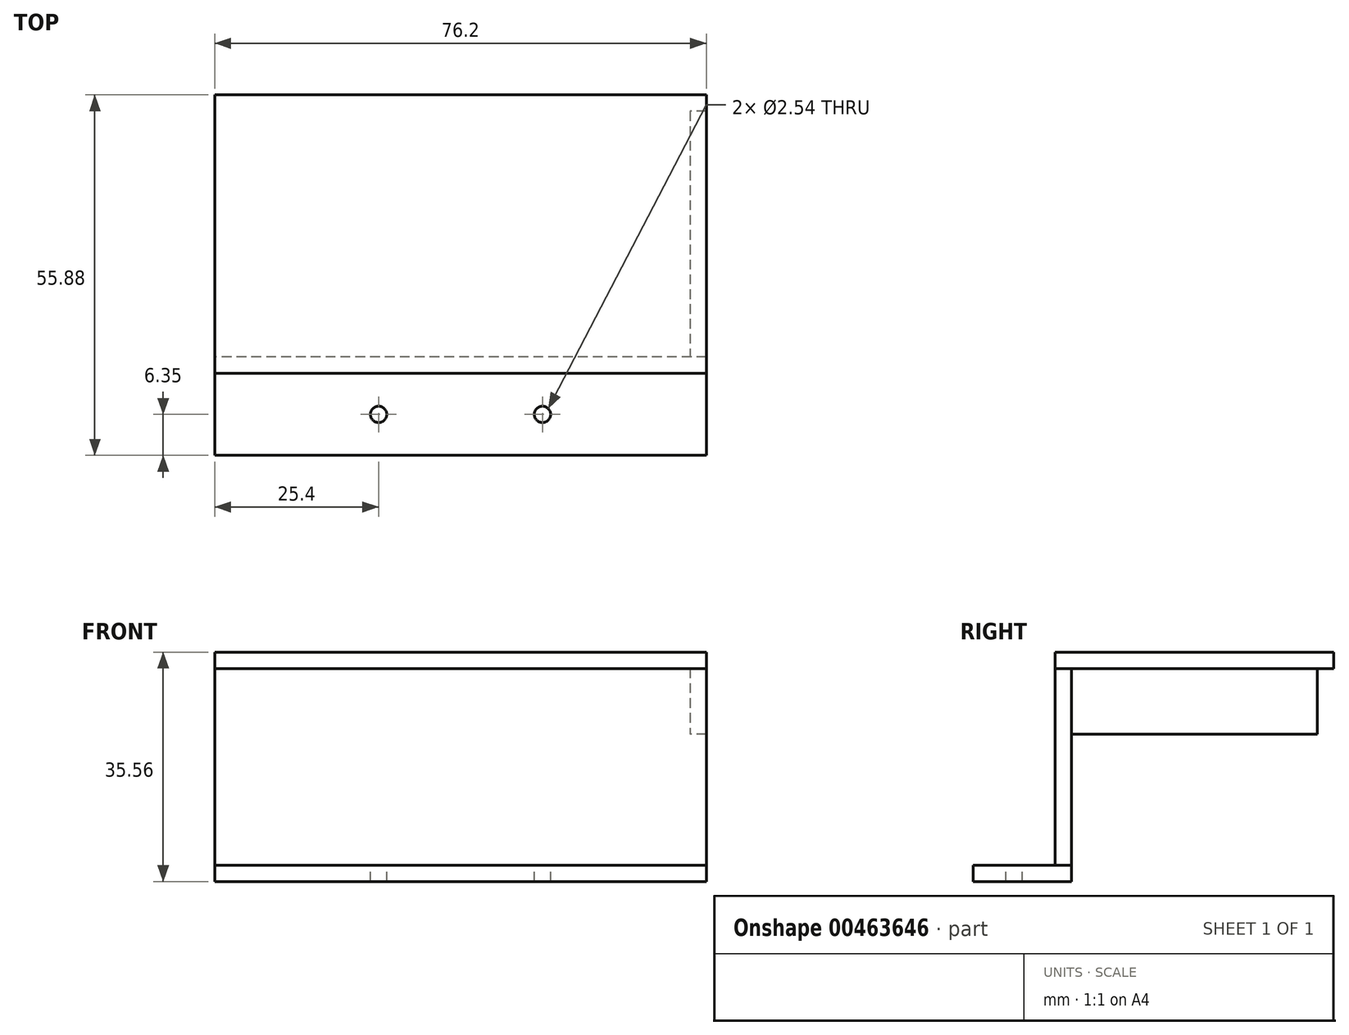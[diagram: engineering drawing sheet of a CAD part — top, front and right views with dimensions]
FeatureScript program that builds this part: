
annotation { "Feature Type Name" : "Feature", "Feature Type Description" : "" }
export const myFeature = defineFeature(function(context is Context, id is Id, definition is map)
    precondition{}
    {
        {
            var Q0;
            Q0=qCreatedBy(makeId("Front.planeOp"),FACE);
            var sketch = newSketch(context, id + "F0", { "sketchPlane" : qUnion([Q0])});
            skLineSegment(sketch, "E0.bottom", {"start": v(38.1, -15.24) * mm, "end": v(-38.1, -15.24) * mm});
            skLineSegment(sketch, "E0.top", {"start": v(38.1, 15.24) * mm, "end": v(-38.1, 15.24) * mm});
            skLineSegment(sketch, "E0.left", {"start": v(38.1, -15.24) * mm, "end": v(38.1, 15.24) * mm});
            skLineSegment(sketch, "E0.right", {"start": v(-38.1, -15.24) * mm, "end": v(-38.1, 15.24) * mm});
            skPoint(sketch, "E0.middle", {"position": v(0, 0) * mm});
            skSolve(sketch);
        }
        {
            var Q0;
            Q0=makeQuery(id+"F0.imprint","IMPRINT",FACE,{"disambiguationData":[TD([[makeQuery(id+"F0.imprint","IMPRINT",EDGE,{"derivedFrom":sQuery(id+"F0.wireOp",EDGE,"E0.bottom")}),-1.0]])]});
            extrude(context, id + "F1", {"entities" : qUnion([Q0]), "depth" : 2.54 * mm});
        }
        {
            var Q0;
            Q0=qCreatedBy(makeId("Right.planeOp"),FACE);
            var sketch = newSketch(context, id + "F2", { "sketchPlane" : qUnion([Q0])});
            skLineSegment(sketch, "E1.bottom", {"start": v(21.59, -5.08) * mm, "end": v(-21.59, -5.08) * mm});
            skLineSegment(sketch, "E1.top", {"start": v(21.59, 5.08) * mm, "end": v(-21.59, 5.08) * mm});
            skLineSegment(sketch, "E1.left", {"start": v(21.59, -5.08) * mm, "end": v(21.59, 5.08) * mm});
            skLineSegment(sketch, "E1.right", {"start": v(-21.59, -5.08) * mm, "end": v(-21.59, 5.08) * mm});
            skPoint(sketch, "E1.middle", {"position": v(0, 0) * mm});
            skSolve(sketch);
        }
        {
            var Q0;
            Q0 = qSketchRegion(id + "F2", true);
            extrude(context, id + "F3", {"entities" : qUnion([Q0]), "depth" : 2.54 * mm});
        }
        {
            var Q0;
            Q0=makeQuery(id+"F3.opExtrude","SWEPT_BODY",BODY,{"disambiguationData":[OSD([sQuery(id+"F2.wireOp",EDGE,"E1.bottom"),sQuery(id+"F2.wireOp",EDGE,"E1.top"),sQuery(id+"F2.wireOp",EDGE,"E1.left"),sQuery(id+"F2.wireOp",EDGE,"E1.right")])]});
            deleteBodies(context, id + "F4", {"entities" : qUnion([Q0])});
        }
        {
            var Q0;
            Q0=makeQuery(id+"F1.opExtrude","CAP_FACE",FACE,{"disambiguationData":[OSD([sQuery(id+"F0.wireOp",EDGE,"E0.bottom"),sQuery(id+"F0.wireOp",EDGE,"E0.top"),sQuery(id+"F0.wireOp",EDGE,"E0.left"),sQuery(id+"F0.wireOp",EDGE,"E0.right")])],"isStart":true});
            var sketch = newSketch(context, id + "F5", { "sketchPlane" : qUnion([Q0])});
            skLineSegment(sketch, "E2.bottom", {"start": v(-38.1, 15.24) * mm, "end": v(-35.56, 15.24) * mm});
            skLineSegment(sketch, "E2.top", {"start": v(-38.1, 5.08) * mm, "end": v(-35.56, 5.08) * mm});
            skLineSegment(sketch, "E2.left", {"start": v(-38.1, 15.24) * mm, "end": v(-38.1, 5.08) * mm});
            skLineSegment(sketch, "E2.right", {"start": v(-35.56, 15.24) * mm, "end": v(-35.56, 5.08) * mm});
            skSolve(sketch);
        }
        {
            var Q0;
            Q0 = qSketchRegion(id + "F5", true);
            extrude(context, id + "F6", {"entities" : qUnion([Q0]), "depth" : 38.1 * mm});
        }
        {
            var Q0;
            Q0=makeQuery(id+"F1.opExtrude","SWEPT_FACE",FACE,{"disambiguationData":[OSD([sQuery(id+"F0.wireOp",EDGE,"E0.top")])]});
            var sketch = newSketch(context, id + "F7", { "sketchPlane" : qUnion([Q0])});
            skLineSegment(sketch, "E3.bottom", {"start": v(38.1, -2.54) * mm, "end": v(-38.1, -2.54) * mm});
            skLineSegment(sketch, "E3.top", {"start": v(38.1, 40.64) * mm, "end": v(-38.1, 40.64) * mm});
            skLineSegment(sketch, "E3.left", {"start": v(38.1, -2.54) * mm, "end": v(38.1, 40.64) * mm});
            skLineSegment(sketch, "E3.right", {"start": v(-38.1, -2.54) * mm, "end": v(-38.1, 40.64) * mm});
            skSolve(sketch);
        }
        {
            var Q0;
            Q0 = qSketchRegion(id + "F7", true);
            extrude(context, id + "F8", {"entities" : qUnion([Q0]), "depth" : 2.54 * mm});
        }
        {
            var Q0;
            Q0=makeQuery(id+"F1.opExtrude","SWEPT_FACE",FACE,{"disambiguationData":[OSD([sQuery(id+"F0.wireOp",EDGE,"E0.bottom")])]});
            var sketch = newSketch(context, id + "F9", { "sketchPlane" : qUnion([Q0])});
            skLineSegment(sketch, "E4.bottom", {"start": v(38.1, 0) * mm, "end": v(-38.1, 0) * mm});
            skLineSegment(sketch, "E4.top", {"start": v(38.1, 15.24) * mm, "end": v(-38.1, 15.24) * mm});
            skLineSegment(sketch, "E4.left", {"start": v(38.1, 0) * mm, "end": v(38.1, 15.24) * mm});
            skLineSegment(sketch, "E4.right", {"start": v(-38.1, 0) * mm, "end": v(-38.1, 15.24) * mm});
            skSolve(sketch);
        }
        {
            var Q0;
            Q0 = qSketchRegion(id + "F9", true);
            extrude(context, id + "F10", {"entities" : qUnion([Q0]), "depth" : 2.54 * mm});
        }
        {
            var Q0;
            Q0=makeQuery(id+"F10.opExtrude","CAP_FACE",FACE,{"disambiguationData":[OSD([sQuery(id+"F9.wireOp",EDGE,"E4.bottom"),sQuery(id+"F9.wireOp",EDGE,"E4.top"),sQuery(id+"F9.wireOp",EDGE,"E4.left"),sQuery(id+"F9.wireOp",EDGE,"E4.right")])],"isStart":true});
            var sketch = newSketch(context, id + "F11", { "sketchPlane" : qUnion([Q0])});
            skLineSegment(sketch, "E5", {"start": v(-38.1, -8.89) * mm, "end": v(-12.7, -8.89) * mm, "construction": true});
            skCircle(sketch, "E6", {"center": v(-12.7, -8.89) * mm, "radius": 1.27 * mm});
            skLineSegment(sketch, "E7", {"start": v(-12.7, -8.89) * mm, "end": v(12.7, -8.89) * mm, "construction": true});
            skCircle(sketch, "E8", {"center": v(12.7, -8.89) * mm, "radius": 1.27 * mm});
            skSolve(sketch);
        }
        {
            var Q0;
            Q0 = qSketchRegion(id + "F11", true);
            extrude(context, id + "F12", {"entities" : qUnion([Q0]), "operationType" : NewBodyOperationType.REMOVE, "oppositeDirection" : true, "depth" : 2.54 * mm});
        }
        {
            var Q0;
            Q0 = qSketchRegion(id + "F11", true);
            extrude(context, id + "F13", {"entities" : qUnion([Q0]), "operationType" : NewBodyOperationType.REMOVE, "oppositeDirection" : true, "depth" : 2.54 * mm});
        }
    });
